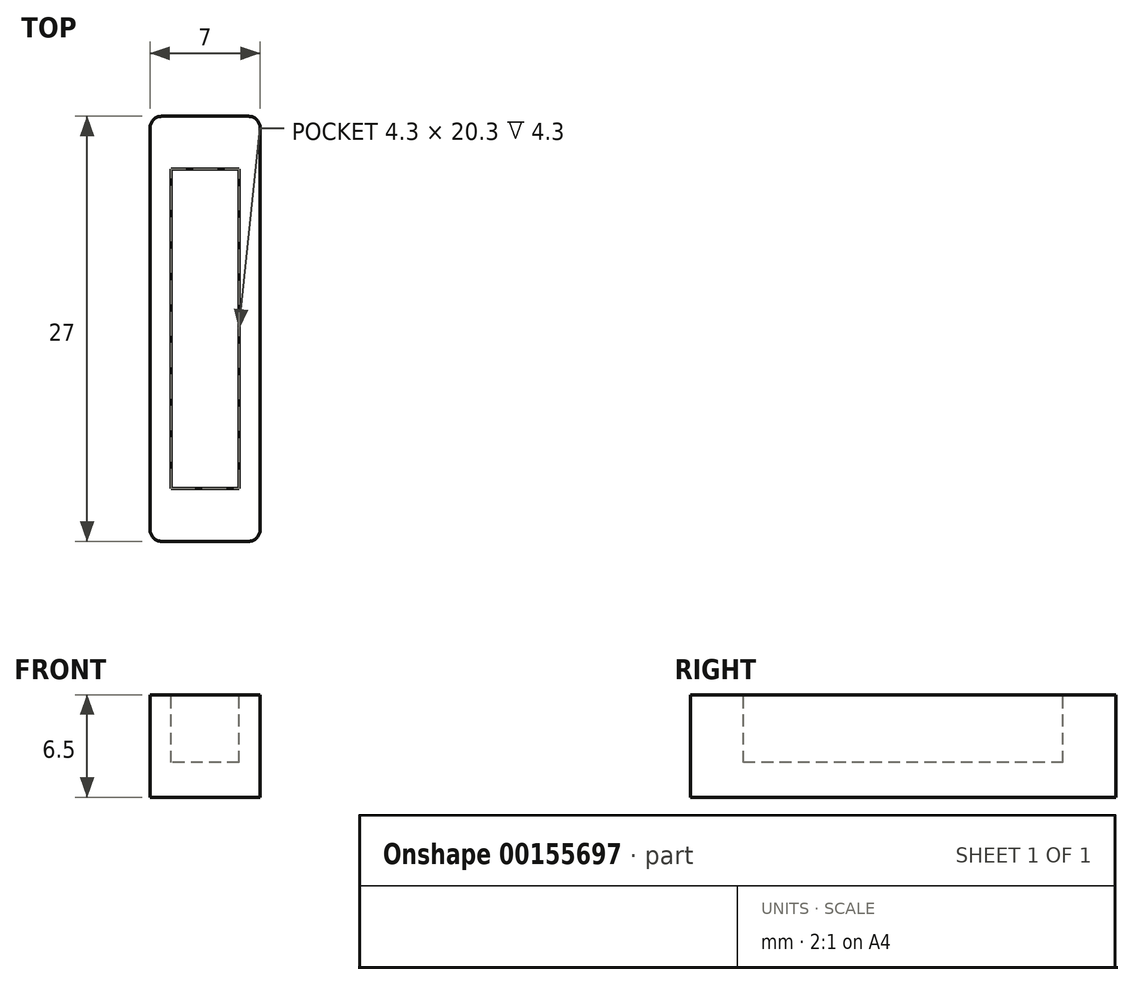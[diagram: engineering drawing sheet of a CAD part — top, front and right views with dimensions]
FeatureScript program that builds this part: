
annotation { "Feature Type Name" : "Feature", "Feature Type Description" : "" }
export const myFeature = defineFeature(function(context is Context, id is Id, definition is map)
    precondition{}
    {
        {
            var Q0;
            Q0=qCreatedBy(makeId("Front.planeOp"),FACE);
            var sketch = newSketch(context, id + "F0", { "sketchPlane" : qUnion([Q0])});
            skLineSegment(sketch, "E0.bottom", {"start": v(3.5, 3.5) * mm, "end": v(-3.5, 3.5) * mm});
            skLineSegment(sketch, "E0.top", {"start": v(3.5, -3.5) * mm, "end": v(-3.5, -3.5) * mm});
            skLineSegment(sketch, "E0.left", {"start": v(3.5, 3.5) * mm, "end": v(3.5, -3.5) * mm});
            skLineSegment(sketch, "E0.right", {"start": v(-3.5, 3.5) * mm, "end": v(-3.5, -3.5) * mm});
            skPoint(sketch, "E0.middle", {"position": v(0, 0) * mm});
            skSolve(sketch);
        }
        {
            var Q0;
            Q0 = qSketchRegion(id + "F0", true);
            extrude(context, id + "F1", {"entities" : qUnion([Q0]), "endBound" : BoundingType.SYMMETRIC, "depth" : 27 * mm});
        }
        {
            var Q0;
            Q0=makeQuery(id+"F1.opExtrude","SWEPT_FACE",FACE,{"disambiguationData":[OSD([sQuery(id+"F0.wireOp",EDGE,"E0.bottom")])]});
            var sketch = newSketch(context, id + "F2", { "sketchPlane" : qUnion([Q0])});
            skLineSegment(sketch, "E1.bottom", {"start": v(2.15, 10.15) * mm, "end": v(-2.15, 10.15) * mm});
            skLineSegment(sketch, "E1.top", {"start": v(2.15, -10.15) * mm, "end": v(-2.15, -10.15) * mm});
            skLineSegment(sketch, "E1.left", {"start": v(2.15, 10.15) * mm, "end": v(2.15, -10.15) * mm});
            skLineSegment(sketch, "E1.right", {"start": v(-2.15, 10.15) * mm, "end": v(-2.15, -10.15) * mm});
            skPoint(sketch, "E1.middle", {"position": v(0, 0) * mm});
            skSolve(sketch);
        }
        {
            var Q0;
            Q0 = qSketchRegion(id + "F2", true);
            extrude(context, id + "F3", {"entities" : qUnion([Q0]), "operationType" : NewBodyOperationType.REMOVE, "oppositeDirection" : true, "depth" : 4.3 * mm});
        }
        {
            var Q0;
            Q0=makeQuery(id+"F1.opExtrude","SWEPT_FACE",FACE,{"disambiguationData":[OSD([sQuery(id+"F0.wireOp",EDGE,"E0.top")])]});
            extrude(context, id + "F4", {"entities" : qUnion([Q0]), "operationType" : NewBodyOperationType.REMOVE, "oppositeDirection" : true, "depth" : 0.5 * mm});
        }
        {
            var Q0;
            Q0=makeQuery(id+"F1.opExtrude","CAP_EDGE",EDGE,{"disambiguationData":[OSD([sQuery(id+"F0.wireOp",EDGE,"E0.right")])],"isStart":true});
            var Q1;
            Q1=makeQuery(id+"F1.opExtrude","CAP_EDGE",EDGE,{"disambiguationData":[OSD([sQuery(id+"F0.wireOp",EDGE,"E0.left")])],"isStart":true});
            var Q2;
            Q2=makeQuery(id+"F1.opExtrude","CAP_EDGE",EDGE,{"disambiguationData":[OSD([sQuery(id+"F0.wireOp",EDGE,"E0.left")])],"isStart":false});
            var Q3;
            Q3=makeQuery(id+"F1.opExtrude","CAP_EDGE",EDGE,{"disambiguationData":[OSD([sQuery(id+"F0.wireOp",EDGE,"E0.right")])],"isStart":false});
            fillet(context, id + "F5", {"entities" : qUnion([Q0, Q1, Q2, Q3]), "radius" : .75 * mm, "tangentPropagation" : true, "allowEdgeOverflow" : false});
        }
    });
